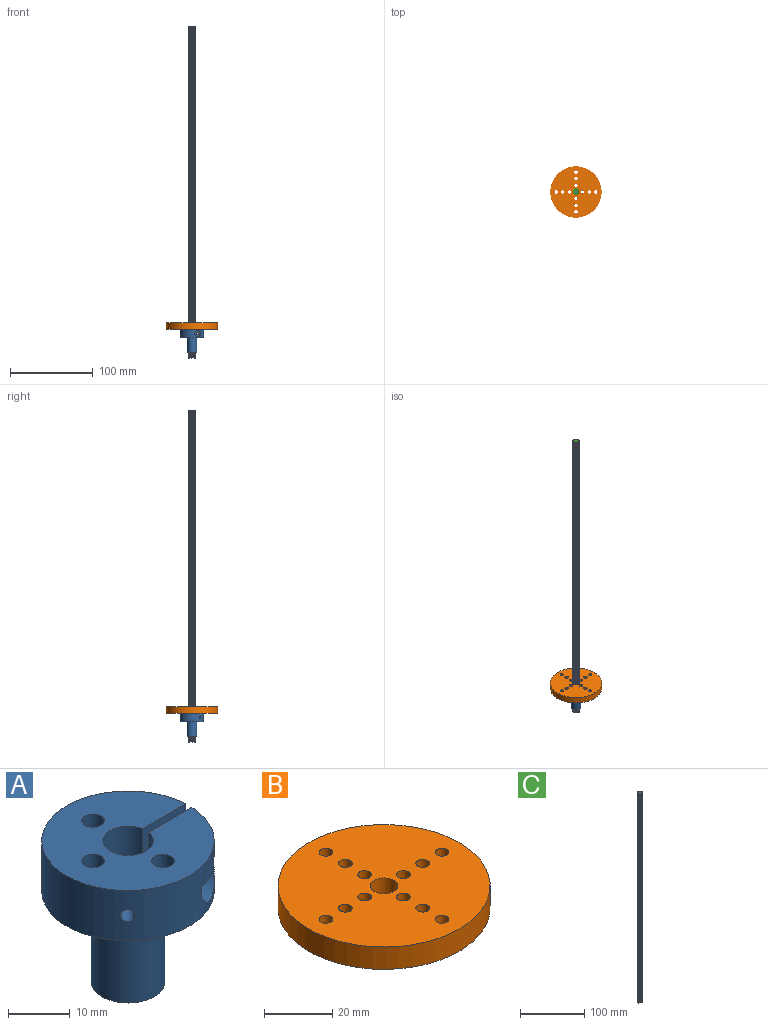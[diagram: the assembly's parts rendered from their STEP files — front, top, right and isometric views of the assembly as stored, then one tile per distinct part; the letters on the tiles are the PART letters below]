
ASSEMBLY  parts=3 mates=2
PART A: 19 faces, bbox 28x28x28 mm
  f0: cylinder r=14mm len=28mm, axis (0,0,-1), area 799.2mm2, adj f2,f4,f9,f10,f11,f12,f16,f17
  f1: cylinder r=4.1mm len=28mm, axis (0,0,-1), area 672.8mm2, adj f2,f4,f5,f9,f17,f18
  f2: plane 28x9.94mm, normal (0,-1,0), area 129.4mm2, adj f0,f1,f3,f5,f9,f10,f16
  f3: cylinder r=6mm len=18mm, axis (0,0,-1), area 653.3mm2, adj f2,f4,f5,f10
  f4: plane 28x9.94mm, normal (0,1,0), area 129.4mm2, adj f0,f1,f3,f5,f9,f10,f15
  f5: plane 12x11.96mm, normal (0,0,-1), area 57.6mm2, adj f1,f2,f3,f4
  f6: cylinder r=1.85mm len=10mm, axis (0,0,-1), area 116.2mm2, adj f9,f10
  f7: cylinder r=1.85mm len=10mm, axis (0,0,-1), area 116.2mm2, adj f9,f10
  f8: cylinder r=1.85mm len=10mm, axis (0,0,-1), area 116.2mm2, adj f9,f10
  f9: plane 28x27.98mm, normal (0,0,1), area 516.8mm2, adj f0,f1,f2,f4,f6,f7,f8
  f10: plane 28x27.98mm, normal (0,0,-1), area 459.2mm2, adj f0,f2,f3,f4,f6,f7,f8
  f11: cylinder r=3.75mm len=7.5mm, axis (0,-1,0), area 64mm2, adj f0,f12
  f12: plane 7.5x7.47mm, normal (0,-1,0), area 35.1mm2, adj f0,f11,f13
  f13: cylinder r=1.7mm len=5.5mm, axis (0,-1,0), area 58.7mm2, adj f12,f14
  f14: plane 3.4x3.4mm, normal (0,-1,0), area 4.6mm2, adj f13,f15
  f15: cylinder r=1.2mm len=2.8mm, axis (0,-1,0), area 21.1mm2, adj f4,f14
  f16: cylinder r=1.2mm len=12.04mm, axis (0,-1,0), area 85.8mm2, adj f0,f2
  f17: cylinder r=1.2mm len=8.79mm, axis (0.71,0.71,0), area 74.9mm2, adj f0,f1
  f18: cylinder r=1.2mm len=8.79mm, axis (0.71,-0.71,0), area 74.9mm2, adj f0,f1
PART B: 16 faces, bbox 62x62x8 mm
  f0: cylinder r=4mm len=8mm, axis (0,0,-1), area 201.1mm2, adj f14,f15
  f1: cylinder r=2mm len=8mm, axis (0,0,-1), area 100.5mm2, adj f14,f15
  f2: cylinder r=2mm len=8mm, axis (0,0,-1), area 100.5mm2, adj f14,f15
  f3: cylinder r=2mm len=8mm, axis (0,0,-1), area 100.5mm2, adj f14,f15
  f4: cylinder r=2mm len=8mm, axis (0,0,-1), area 100.5mm2, adj f14,f15
  f5: cylinder r=2mm len=8mm, axis (0,0,-1), area 100.5mm2, adj f14,f15
  f6: cylinder r=2mm len=8mm, axis (0,0,-1), area 100.5mm2, adj f14,f15
  f7: cylinder r=2mm len=8mm, axis (0,0,-1), area 100.5mm2, adj f14,f15
  f8: cylinder r=2mm len=8mm, axis (0,0,-1), area 100.5mm2, adj f14,f15
  f9: cylinder r=2mm len=8mm, axis (0,0,-1), area 100.5mm2, adj f14,f15
  f10: cylinder r=2mm len=8mm, axis (0,0,-1), area 100.5mm2, adj f14,f15
  f11: cylinder r=2mm len=8mm, axis (0,0,-1), area 100.5mm2, adj f14,f15
  f12: cylinder r=2mm len=8mm, axis (0,0,-1), area 100.5mm2, adj f14,f15
  f13: cylinder r=31mm len=62mm, axis (0,0,-1), area 1558.2mm2, adj f14,f15
  f14: plane 62x62mm, normal (0,0,1), area 2818mm2, adj f0,f1,f2,f3,f4,f5,f6,f7
  f15: plane 62x62mm, normal (0,0,-1), area 2818mm2, adj f0,f1,f2,f3,f4,f5,f6,f7
PART C: 34 faces, bbox 8x8x401 mm
  f0: plane 7x7mm, normal (0,0,-1), area 35.9mm2, adj f1,f2,f3,f7,f8,f9,f12,f14
  f1: cylinder r=3.5mm len=400mm, axis (0,0,-1), area 1150.5mm2, adj f0,f4,f17,f19,f22,f26
  f2: cylinder r=3.5mm len=400mm, axis (0,0,-1), area 1150.5mm2, adj f0,f4,f16,f18,f28,f29
  f3: cylinder r=3.5mm len=400mm, axis (0,0,-1), area 1150.5mm2, adj f0,f4,f6,f7,f27,f30
  f4: plane 7x7mm, normal (0,0,1), area 35.9mm2, adj f1,f2,f3,f5,f6,f11,f12,f15
  f5: plane 1x1mm, normal (0,1,0), area 0.8mm2, adj f4,f6,f8,f10,f11,f12
  f6: bspline ~400x8mm, area 624.7mm2, adj f3,f4,f5,f7,f10,f11
  f7: plane 1x1mm, normal (0,-1,0), area 0.7mm2, adj f0,f3,f6,f8,f9,f10
  f8: bspline ~400x8mm, area 623.5mm2, adj f0,f5,f7,f9,f10,f12
  f9: cylinder r=3mm len=1.15mm, axis (0,0,1), area 0.3mm2, adj f0,f7,f8
  f10: cylinder r=4mm len=401mm, axis (0,0,1), area 1256.6mm2, adj f5,f6,f7,f8
  f11: cylinder r=3mm len=1.15mm, axis (0,0,1), area 0.3mm2, adj f4,f5,f6
  f12: cylinder r=3.5mm len=400mm, axis (0,0,-1), area 1150.5mm2, adj f0,f4,f5,f8,f23,f25
  f13: cylinder r=4mm len=401mm, axis (0,0,1), area 1256.6mm2, adj f16,f17,f18,f19
  f14: cylinder r=3mm len=1.15mm, axis (0,0,1), area 0.3mm2, adj f0,f18,f19
  f15: cylinder r=3mm len=1.15mm, axis (0,0,1), area 0.3mm2, adj f4,f16,f17
  f16: plane 1x1mm, normal (0,-1,0), area 0.8mm2, adj f2,f4,f13,f15,f17,f18
  f17: bspline ~400x8mm, area 624.7mm2, adj f1,f4,f13,f15,f16,f19
  f18: bspline ~400x8mm, area 623.5mm2, adj f0,f2,f13,f14,f16,f19
  f19: plane 1x1mm, normal (0,1,0), area 0.7mm2, adj f0,f1,f13,f14,f17,f18
  f20: cylinder r=4mm len=401mm, axis (0,0,1), area 1256.6mm2, adj f22,f23,f25,f26
  f21: cylinder r=3mm len=1.15mm, axis (0,0,1), area 0.3mm2, adj f4,f22,f23
  f22: plane 1x1mm, normal (-1,0,0), area 0.8mm2, adj f1,f4,f20,f21,f23,f26
  f23: bspline ~400x8mm, area 624.7mm2, adj f4,f12,f20,f21,f22,f25
  f24: cylinder r=3mm len=1.15mm, axis (0,0,1), area 0.3mm2, adj f0,f25,f26
  f25: plane 1x1mm, normal (1,0,0), area 0.7mm2, adj f0,f12,f20,f23,f24,f26
  f26: bspline ~400x8mm, area 623.5mm2, adj f0,f1,f20,f22,f24,f25
  f27: plane 1x1mm, normal (1,0,0), area 0.8mm2, adj f3,f4,f28,f30,f32,f33
  f28: bspline ~400x8mm, area 624.7mm2, adj f2,f4,f27,f29,f32,f33
  f29: plane 1x1mm, normal (-1,0,0), area 0.7mm2, adj f0,f2,f28,f30,f31,f32
  f30: bspline ~400x8mm, area 623.5mm2, adj f0,f3,f27,f29,f31,f32
  f31: cylinder r=3mm len=1.15mm, axis (0,0,1), area 0.3mm2, adj f0,f29,f30
  f32: cylinder r=4mm len=401mm, axis (0,0,1), area 1256.6mm2, adj f27,f28,f29,f30
  f33: cylinder r=3mm len=1.15mm, axis (0,0,1), area 0.3mm2, adj f4,f27,f28
PLACE A t=(-20.84,33.15,14.6)mm
PLACE B t=(-20.84,33.15,42.6)mm
PLACE C t=(-20.84,33.15,8.6)mm
MATE fastened B.f0 <-> A.f0  axis (0,0,-1) through (-20.84,33.15,42.6)mm
MATE fastened C.f1 <-> A.f1  axis (0,0,-1) through (-20.84,33.15,8.6)mm
